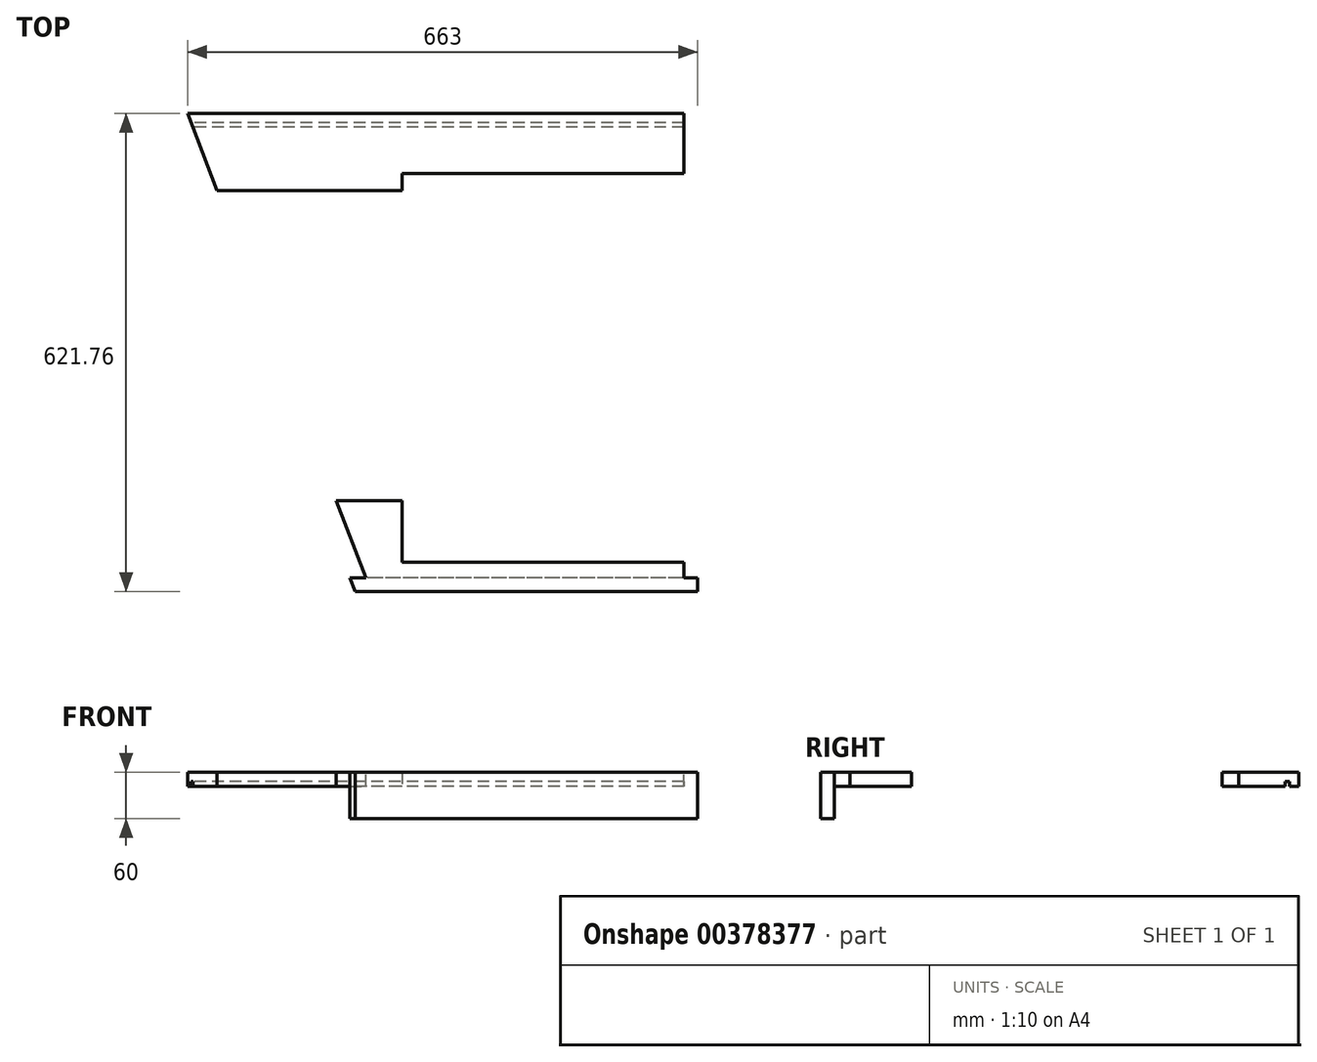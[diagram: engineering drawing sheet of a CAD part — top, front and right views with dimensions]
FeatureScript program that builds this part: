
annotation { "Feature Type Name" : "Feature", "Feature Type Description" : "" }
export const myFeature = defineFeature(function(context is Context, id is Id, definition is map)
    precondition{}
    {
        {
            var Q0;
            Q0=qCreatedBy(makeId("Top.planeOp"),FACE);
            var sketch = newSketch(context, id + "F0", { "sketchPlane" : qUnion([Q0])});
            skLineSegment(sketch, "E0.bottom", {"start": v(322.5, 310.88) * mm, "end": v(-322.5, 310.88) * mm});
            skLineSegment(sketch, "E0.top", {"start": v(322.5, -310.88) * mm, "end": v(-83.83, -310.88) * mm});
            skLineSegment(sketch, "E0.left", {"start": v(322.5, 310.88) * mm, "end": v(322.5, 210.88) * mm});
            skPoint(sketch, "E0.middle", {"position": v(0, 0) * mm});
            skLineSegment(sketch, "E1", {"start": v(-322.5, 310.88) * mm, "end": v(-284.11, 210.88) * mm});
            skLineSegment(sketch, "E2.0", {"start": v(322.5, 210.88) * mm, "end": v(-284.11, 210.88) * mm});
            skLineSegment(sketch, "E3.0", {"start": v(322.5, -192.88) * mm, "end": v(-129.12, -192.88) * mm});
            skLineSegment(sketch, "E4.trimOffspring", {"start": v(-129.12, -192.88) * mm, "end": v(-83.83, -310.88) * mm});
            skLineSegment(sketch, "E5.trimOffspring", {"start": v(322.5, -192.88) * mm, "end": v(322.5, -310.88) * mm});
            skSolve(sketch);
        }
        {
            var Q0;
            Q0=qSketchRegion(id+"F0",true);
            extrude(context, id + "F1", {"entities" : qUnion([Q0]), "depth" : 18 * mm});
        }
        {
            var Q0;
            Q0=makeQuery(id+"F1.opExtrude","CAP_FACE",FACE,{"disambiguationData":[OSD([sQuery(id+"F0.wireOp",EDGE,"E0.bottom"),sQuery(id+"F0.wireOp",EDGE,"E0.left"),sQuery(id+"F0.wireOp",EDGE,"E1"),sQuery(id+"F0.wireOp",EDGE,"E2.0")])],"isStart":true});
            var sketch = newSketch(context, id + "F2", { "sketchPlane" : qUnion([Q0])});
            skLineSegment(sketch, "E6.bottom", {"start": v(322.5, -292.88) * mm, "end": v(-317.9, -292.88) * mm});
            skLineSegment(sketch, "E6.top", {"start": v(322.5, -298.88) * mm, "end": v(-317.9, -298.88) * mm});
            skLineSegment(sketch, "E6.left", {"start": v(322.5, -292.88) * mm, "end": v(322.5, -298.88) * mm});
            skLineSegment(sketch, "E6.right", {"start": v(-317.9, -292.88) * mm, "end": v(-317.9, -298.88) * mm});
            skSolve(sketch);
        }
        {
            var Q0;
            Q0 = qSketchRegion(id + "F2", true);
            extrude(context, id + "F3", {"entities" : qUnion([Q0]), "operationType" : NewBodyOperationType.REMOVE, "oppositeDirection" : true, "depth" : 6 * mm});
        }
        {
            var Q0;
            Q0=makeQuery(id+"F1.opExtrude","CAP_FACE",FACE,{"disambiguationData":[OSD([sQuery(id+"F0.wireOp",EDGE,"E0.top"),sQuery(id+"F0.wireOp",EDGE,"E3.0"),sQuery(id+"F0.wireOp",EDGE,"E4.trimOffspring"),sQuery(id+"F0.wireOp",EDGE,"E5.trimOffspring")])],"isStart":true});
            var sketch = newSketch(context, id + "F4", { "sketchPlane" : qUnion([Q0])});
            skLineSegment(sketch, "E7", {"start": v(-83.83, 310.88) * mm, "end": v(322.5, 310.88) * mm});
            skLineSegment(sketch, "E8", {"start": v(322.5, 310.88) * mm, "end": v(322.5, 292.88) * mm});
            skLineSegment(sketch, "E9", {"start": v(322.5, 292.88) * mm, "end": v(-90.74, 292.88) * mm});
            skLineSegment(sketch, "E10", {"start": v(-90.74, 292.88) * mm, "end": v(-83.83, 310.88) * mm});
            skSolve(sketch);
        }
        {
            var Q0;
            Q0 = qSketchRegion(id + "F4", true);
            extrude(context, id + "F5", {"entities" : qUnion([Q0]), "operationType" : NewBodyOperationType.ADD, "depth" : 42 * mm});
        }
        {
            var Q0;
            Q0=makeQuery(id+"F5.boolean.opBoolean","MERGE",FACE,{"derivedFrom":[makeQuery(id+"F1.opExtrude","SWEPT_FACE",FACE,{"disambiguationData":[OSD([sQuery(id+"F0.wireOp",EDGE,"E5.trimOffspring")])]}),makeQuery(id+"F5.opExtrude","SWEPT_FACE",FACE,{"disambiguationData":[OSD([sQuery(id+"F4.wireOp",EDGE,"E8")])]})]});
            var sketch = newSketch(context, id + "F6", { "sketchPlane" : qUnion([Q0])});
            skLineSegment(sketch, "E11", {"start": v(-310.88, -42) * mm, "end": v(-310.88, 18) * mm});
            skLineSegment(sketch, "E12", {"start": v(-310.88, 18) * mm, "end": v(-292.88, 18) * mm});
            skLineSegment(sketch, "E13", {"start": v(-292.88, 18) * mm, "end": v(-292.88, -42) * mm});
            skLineSegment(sketch, "E14", {"start": v(-292.88, -42) * mm, "end": v(-310.88, -42) * mm});
            skSolve(sketch);
        }
        {
            var Q0;
            Q0 = qSketchRegion(id + "F6", true);
            extrude(context, id + "F7", {"entities" : qUnion([Q0]), "operationType" : NewBodyOperationType.ADD, "depth" : 18 * mm, "hasSecondDirection" : true, "secondDirectionOppositeDirection" : true, "secondDirectionDepth" : 434 * mm});
        }
        {
            var Q0;
            Q0=makeQuery(id+"F7.boolean.opBoolean","MERGE",FACE,{"derivedFrom":[makeQuery(id+"F1.opExtrude","CAP_FACE",FACE,{"disambiguationData":[OSD([sQuery(id+"F0.wireOp",EDGE,"E0.top"),sQuery(id+"F0.wireOp",EDGE,"E3.0"),sQuery(id+"F0.wireOp",EDGE,"E4.trimOffspring"),sQuery(id+"F0.wireOp",EDGE,"E5.trimOffspring")])],"isStart":false}),makeQuery(id+"F7.opExtrude","SWEPT_FACE",FACE,{"disambiguationData":[OSD([sQuery(id+"F6.wireOp",EDGE,"E12")])]})]});
            var sketch = newSketch(context, id + "F8", { "sketchPlane" : qUnion([Q0])});
            skLineSegment(sketch, "E15", {"start": v(-111.5, -292.88) * mm, "end": v(-104.6, -310.88) * mm});
            skLineSegment(sketch, "E16", {"start": v(-104.6, -310.88) * mm, "end": v(-111.5, -310.88) * mm});
            skLineSegment(sketch, "E17", {"start": v(-111.5, -310.88) * mm, "end": v(-111.5, -292.88) * mm});
            skSolve(sketch);
        }
        {
            var Q0;
            Q0=makeQuery(id+"F7.boolean.opBoolean","MERGE",FACE,{"derivedFrom":[makeQuery(id+"F1.opExtrude","CAP_FACE",FACE,{"disambiguationData":[OSD([sQuery(id+"F0.wireOp",EDGE,"E0.top"),sQuery(id+"F0.wireOp",EDGE,"E3.0"),sQuery(id+"F0.wireOp",EDGE,"E4.trimOffspring"),sQuery(id+"F0.wireOp",EDGE,"E5.trimOffspring")])],"isStart":false}),makeQuery(id+"F7.opExtrude","SWEPT_FACE",FACE,{"disambiguationData":[OSD([sQuery(id+"F6.wireOp",EDGE,"E12")])]})]});
            var sketch = newSketch(context, id + "F9", { "sketchPlane" : qUnion([Q0])});
            skLineSegment(sketch, "E18.bottom", {"start": v(322.5, 232.88) * mm, "end": v(-43.5, 232.88) * mm});
            skLineSegment(sketch, "E18.top", {"start": v(322.5, -272.88) * mm, "end": v(-43.5, -272.88) * mm});
            skLineSegment(sketch, "E18.left", {"start": v(322.5, 232.88) * mm, "end": v(322.5, -272.88) * mm});
            skLineSegment(sketch, "E18.right", {"start": v(-43.5, 232.88) * mm, "end": v(-43.5, -272.88) * mm});
            skPoint(sketch, "E19.orphan", {"position": v(0, -272.88) * mm});
            skSolve(sketch);
        }
        {
            var Q0;
            Q0 = qSketchRegion(id + "F8", true);
            extrude(context, id + "F10", {"entities" : qUnion([Q0]), "operationType" : NewBodyOperationType.REMOVE, "oppositeDirection" : true, "depth" : 60 * mm});
        }
        {
            var Q0;
            Q0 = qSketchRegion(id + "F9", true);
            extrude(context, id + "F11", {"entities" : qUnion([Q0]), "operationType" : NewBodyOperationType.REMOVE, "oppositeDirection" : true, "depth" : 18 * mm});
        }
    });
